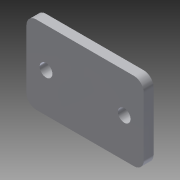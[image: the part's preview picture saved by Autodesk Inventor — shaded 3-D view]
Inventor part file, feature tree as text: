
AUTODESK INVENTOR PART (.ipt)
format: ipt  version: 2014 (Build 180170000, 170)  size: 91,136 bytes
history: native  units: in
note: dims shown in document units (in); Inventor stores cm internally (conversion verified against a paired STEP export)
features: extrude x1, fillet x1, sketch x1
ambient origin geometry x8: Origin, YZ Plane, XZ Plane, XY Plane, X Axis, Y Axis, Z Axis, Center Point
bodies: Solid1 (feature_tree)
feature tree (3):
  extrude  "Extrusion1"  Depth=1.0in
  fillet  "Fillet1"  Radius=0.163in
  sketch  "Sketch1"  dims[d0=1.5in d1=1.0in d2=0.163in d3=0.25in d4=0.5in d12=0.125in d13=0.0in d14=0.125in d22=0.7874in d24=1.0in d25=0.3937in d27=1.0in]
